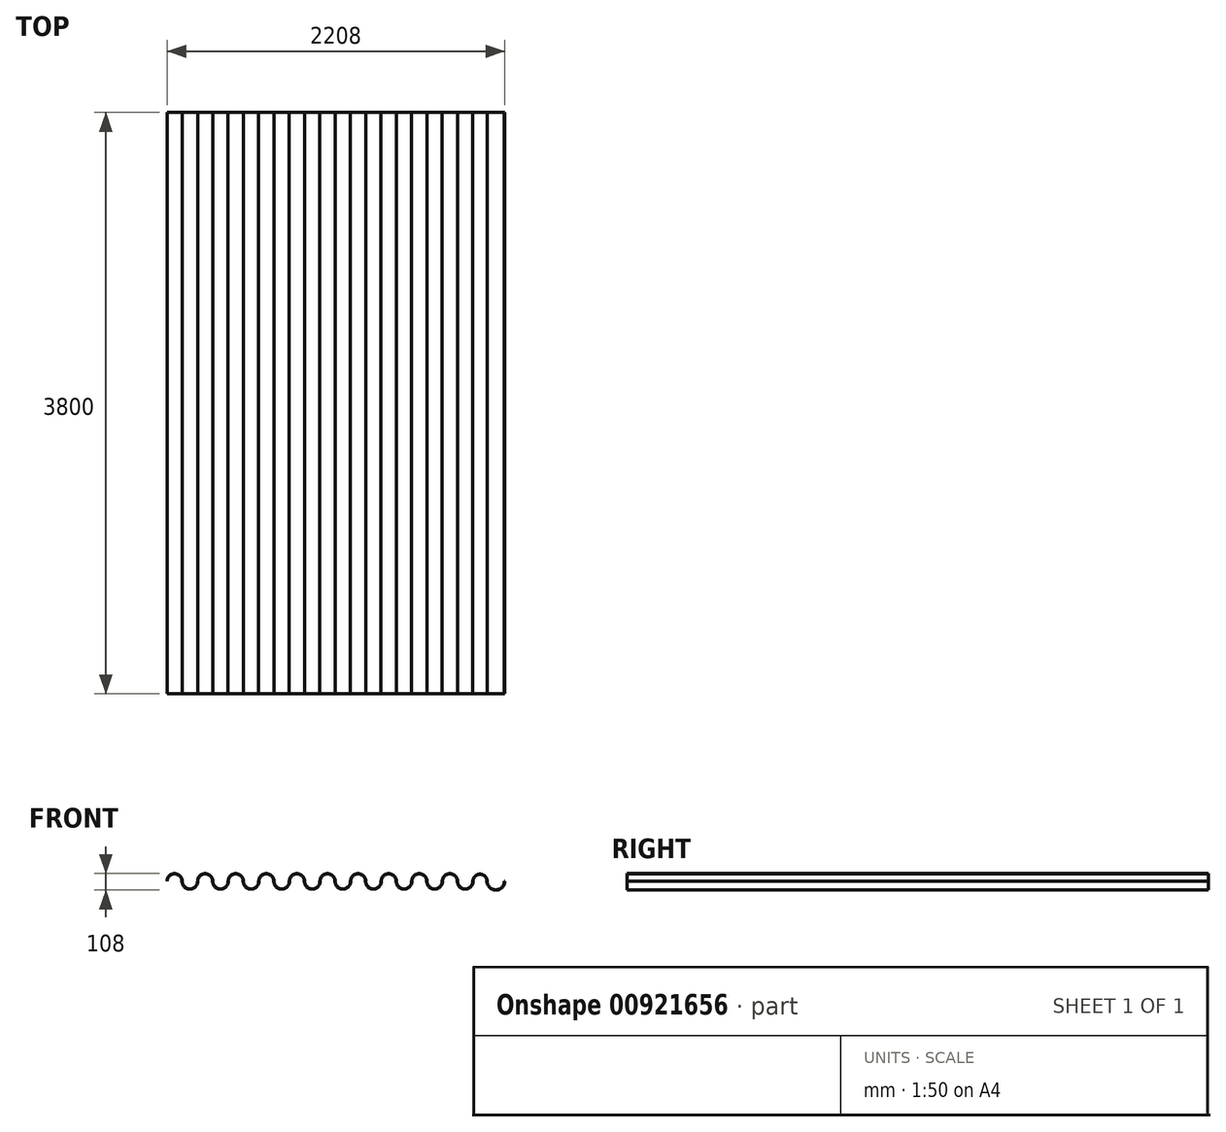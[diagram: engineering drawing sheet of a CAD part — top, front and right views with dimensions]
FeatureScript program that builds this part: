
annotation { "Feature Type Name" : "Feature", "Feature Type Description" : "" }
export const myFeature = defineFeature(function(context is Context, id is Id, definition is map)
    precondition{}
    {
        {
            var Q0;
            Q0=qCreatedBy(makeId("Front.planeOp"),FACE);
            var sketch = newSketch(context, id + "F0", { "sketchPlane" : qUnion([Q0])});
            skArc(sketch, "E0", {"start": v(50, 0) * mm, "mid": v(0, 50) * mm, "end": v(-50, 0) * mm});
            skArc(sketch, "E1", {"start": v(50, 0) * mm, "mid": v(100, -50) * mm, "end": v(150, 0) * mm});
            skArc(sketch, "E2", {"start": v(150, 0) * mm, "mid": v(200, 50) * mm, "end": v(250, 0) * mm});
            skArc(sketch, "E3", {"start": v(250, 0) * mm, "mid": v(300, -50) * mm, "end": v(350, 0) * mm});
            skArc(sketch, "E4", {"start": v(350, 0) * mm, "mid": v(400, 50) * mm, "end": v(450, 0) * mm});
            skArc(sketch, "E5", {"start": v(450, 0) * mm, "mid": v(500, -50) * mm, "end": v(550, 0) * mm});
            skArc(sketch, "E6", {"start": v(550, 0) * mm, "mid": v(600, 50) * mm, "end": v(650, 0) * mm});
            skArc(sketch, "E7", {"start": v(650, 0) * mm, "mid": v(700, -50) * mm, "end": v(750, 0) * mm});
            skArc(sketch, "E8", {"start": v(750, 0) * mm, "mid": v(800, 50) * mm, "end": v(850, 0) * mm});
            skArc(sketch, "E9", {"start": v(850, 0) * mm, "mid": v(900, -50) * mm, "end": v(950, 0) * mm});
            skArc(sketch, "E10", {"start": v(950, 0) * mm, "mid": v(1000, 50) * mm, "end": v(1050, 0) * mm});
            skArc(sketch, "E11", {"start": v(1050, 0) * mm, "mid": v(1100, -50) * mm, "end": v(1150, 0) * mm});
            skArc(sketch, "E12", {"start": v(1150, 0) * mm, "mid": v(1200, 50) * mm, "end": v(1250, 0) * mm});
            skArc(sketch, "E13", {"start": v(1250, 0) * mm, "mid": v(1300, -50) * mm, "end": v(1350, 0) * mm});
            skArc(sketch, "E14", {"start": v(1350, 0) * mm, "mid": v(1400, 50) * mm, "end": v(1450, 0) * mm});
            skArc(sketch, "E15", {"start": v(1450, 0) * mm, "mid": v(1500, -50) * mm, "end": v(1550, 0) * mm});
            skArc(sketch, "E16", {"start": v(1550, 0) * mm, "mid": v(1600, 50) * mm, "end": v(1650, 0) * mm});
            skArc(sketch, "E17", {"start": v(1650, 0) * mm, "mid": v(1700, -50) * mm, "end": v(1750, 0) * mm});
            skArc(sketch, "E18", {"start": v(1750, 0) * mm, "mid": v(1800, 50) * mm, "end": v(1850, 0) * mm});
            skArc(sketch, "E19", {"start": v(1850, 0) * mm, "mid": v(1900, -50) * mm, "end": v(1950, 0) * mm});
            skArc(sketch, "E20", {"start": v(1950, 0) * mm, "mid": v(1997, 47) * mm, "end": v(2044, 0) * mm});
            skArc(sketch, "E21", {"start": v(2044, 0) * mm, "mid": v(2100, -56) * mm, "end": v(2156, 0) * mm});
            skArc(sketch, "E22.0", {"start": v(2042, 0) * mm, "mid": v(2100, -58) * mm, "end": v(2158, 0) * mm});
            skArc(sketch, "E22.1", {"start": v(1952, 0) * mm, "mid": v(1997, 45) * mm, "end": v(2042, 0) * mm});
            skArc(sketch, "E22.2", {"start": v(1848, 0) * mm, "mid": v(1900, -52) * mm, "end": v(1952, 0) * mm});
            skArc(sketch, "E22.3", {"start": v(1752, 0) * mm, "mid": v(1800, 48) * mm, "end": v(1848, 0) * mm});
            skArc(sketch, "E22.4", {"start": v(1648, 0) * mm, "mid": v(1700, -52) * mm, "end": v(1752, 0) * mm});
            skArc(sketch, "E22.5", {"start": v(1552, 0) * mm, "mid": v(1600, 48) * mm, "end": v(1648, 0) * mm});
            skArc(sketch, "E22.6", {"start": v(1448, 0) * mm, "mid": v(1500, -52) * mm, "end": v(1552, 0) * mm});
            skArc(sketch, "E22.7", {"start": v(1352, 0) * mm, "mid": v(1400, 48) * mm, "end": v(1448, 0) * mm});
            skArc(sketch, "E22.8", {"start": v(1248, 0) * mm, "mid": v(1300, -52) * mm, "end": v(1352, 0) * mm});
            skArc(sketch, "E22.9", {"start": v(1152, 0) * mm, "mid": v(1200, 48) * mm, "end": v(1248, 0) * mm});
            skArc(sketch, "E22.10", {"start": v(1048, 0) * mm, "mid": v(1100, -52) * mm, "end": v(1152, 0) * mm});
            skArc(sketch, "E22.11", {"start": v(952, 0) * mm, "mid": v(1000, 48) * mm, "end": v(1048, 0) * mm});
            skArc(sketch, "E22.12", {"start": v(248, 0) * mm, "mid": v(300, -52) * mm, "end": v(352, 0) * mm});
            skArc(sketch, "E22.13", {"start": v(152, 0) * mm, "mid": v(200, 48) * mm, "end": v(248, 0) * mm});
            skArc(sketch, "E22.14", {"start": v(48, 0) * mm, "mid": v(100, -52) * mm, "end": v(152, 0) * mm});
            skArc(sketch, "E22.15", {"start": v(48, 0) * mm, "mid": v(0, 48) * mm, "end": v(-48, 0) * mm});
            skArc(sketch, "E22.16", {"start": v(352, 0) * mm, "mid": v(400, 48) * mm, "end": v(448, 0) * mm});
            skArc(sketch, "E22.17", {"start": v(448, 0) * mm, "mid": v(500, -52) * mm, "end": v(552, 0) * mm});
            skArc(sketch, "E22.18", {"start": v(552, 0) * mm, "mid": v(600, 48) * mm, "end": v(648, 0) * mm});
            skArc(sketch, "E22.19", {"start": v(648, 0) * mm, "mid": v(700, -52) * mm, "end": v(752, 0) * mm});
            skArc(sketch, "E22.20", {"start": v(752, 0) * mm, "mid": v(800, 48) * mm, "end": v(848, 0) * mm});
            skArc(sketch, "E22.21", {"start": v(848, 0) * mm, "mid": v(900, -52) * mm, "end": v(952, 0) * mm});
            skLineSegment(sketch, "E23", {"start": v(2156, 0) * mm, "end": v(2158, 0) * mm});
            skLineSegment(sketch, "E24", {"start": v(-50, 0) * mm, "end": v(-48, 0) * mm});
            skSolve(sketch);
        }
        {
            var Q0;
            Q0=qSketchRegion(id+"F0",true);
            extrude(context, id + "F1", {"entities" : qUnion([Q0]), "depth" : 3800 * mm, "offsetDistance" : 25 * mm});
        }
    });
